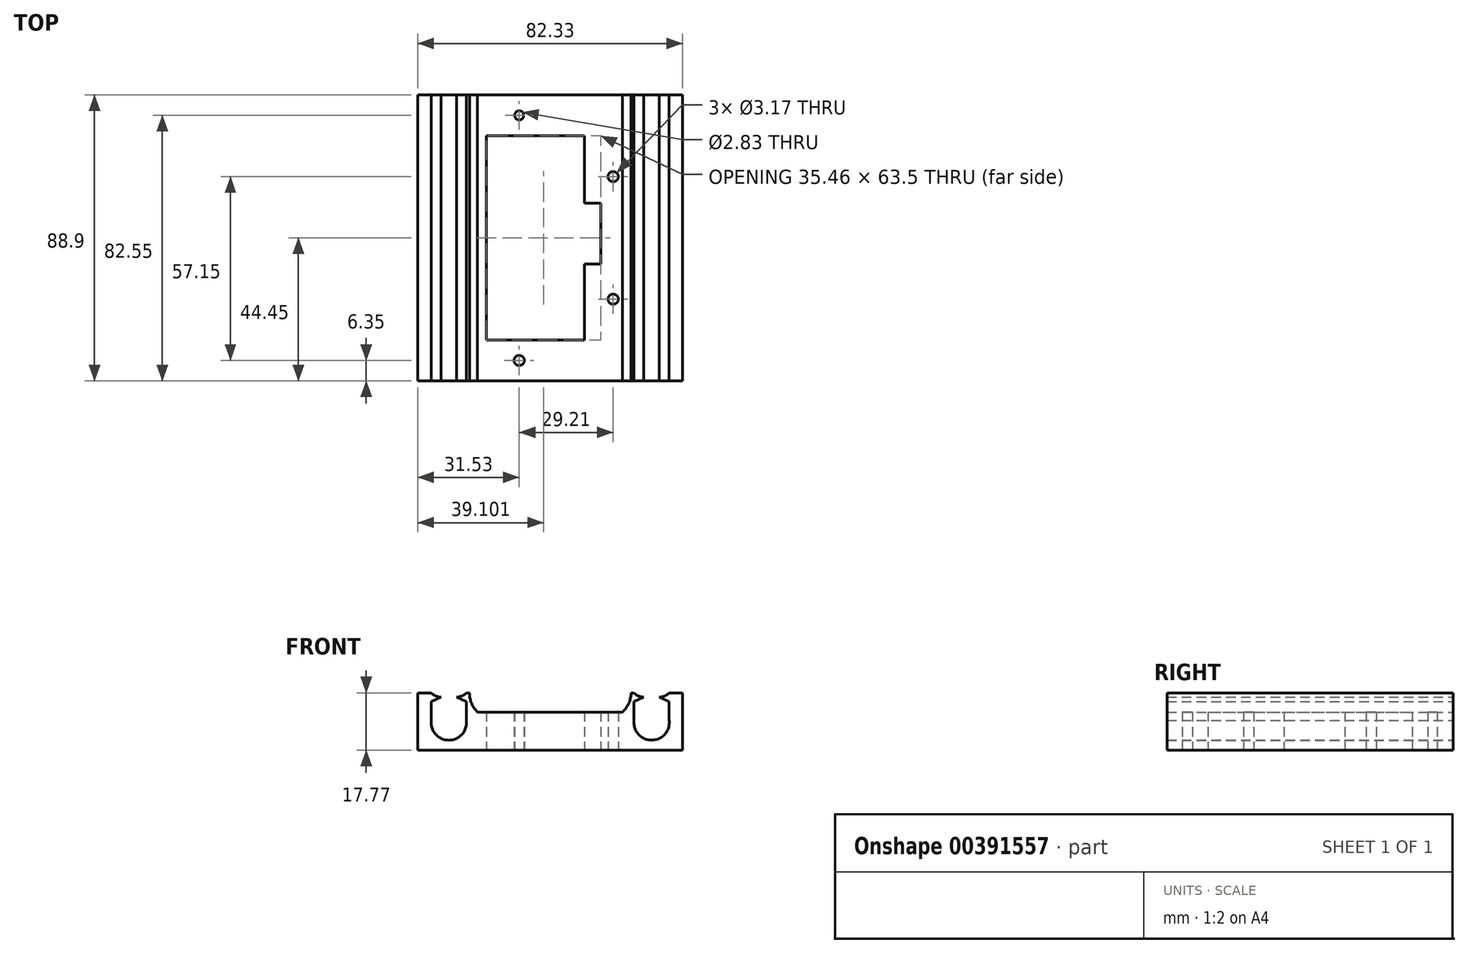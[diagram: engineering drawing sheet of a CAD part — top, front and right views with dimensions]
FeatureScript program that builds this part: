
annotation { "Feature Type Name" : "Feature", "Feature Type Description" : "" }
export const myFeature = defineFeature(function(context is Context, id is Id, definition is map)
    precondition{}
    {
        {
            var Q0;
            Q0=qCreatedBy(makeId("Front.planeOp"),FACE);
            var sketch = newSketch(context, id + "F0", { "sketchPlane" : qUnion([Q0])});
            skLineSegment(sketch, "E0.left", {"start": v(0, 0) * mm, "end": v(0, 17.77) * mm});
            skLineSegment(sketch, "E1", {"start": v(0, 0) * mm, "end": v(-22.84, 0) * mm});
            skLineSegment(sketch, "E2", {"start": v(-78.15, 17.77) * mm, "end": v(-78.15, 9.24) * mm});
            skLineSegment(sketch, "E3", {"start": v(-67.22, 17.77) * mm, "end": v(-67.22, 9.24) * mm});
            skArc(sketch, "E4", {"start": v(-78.15, 9.24) * mm, "mid": v(-72.68, 3.06) * mm, "end": v(-67.22, 9.24) * mm});
            skLineSegment(sketch, "E5", {"start": v(-66.27, 17.77) * mm, "end": v(-66.27, 11.8) * mm});
            skLineSegment(sketch, "E6", {"start": v(-66.27, 11.8) * mm, "end": v(-16.06, 11.8) * mm});
            skLineSegment(sketch, "E7", {"start": v(-16.06, 11.8) * mm, "end": v(-16.06, 17.77) * mm});
            skLineSegment(sketch, "E8", {"start": v(-67.22, 17.77) * mm, "end": v(-66.27, 17.77) * mm});
            skLineSegment(sketch, "E9", {"start": v(-16.06, 17.77) * mm, "end": v(-15.12, 17.77) * mm});
            skLineSegment(sketch, "E10", {"start": v(-15.12, 17.77) * mm, "end": v(-15.12, 9.28) * mm});
            skLineSegment(sketch, "E11", {"start": v(-4.2, 17.77) * mm, "end": v(-4.2, 9.3) * mm});
            skArc(sketch, "E12", {"start": v(-15.12, 9.28) * mm, "mid": v(-9.65, 3.1) * mm, "end": v(-4.2, 9.3) * mm});
            skLineSegment(sketch, "E13", {"start": v(-4.2, 17.77) * mm, "end": v(0, 17.77) * mm});
            skLineSegment(sketch, "E14", {"start": v(0, 17.77) * mm, "end": v(-4.2, 17.77) * mm});
            skLineSegment(sketch, "E15", {"start": v(-78.15, 17.77) * mm, "end": v(-82.33, 17.77) * mm});
            skLineSegment(sketch, "E16", {"start": v(-82.33, 17.77) * mm, "end": v(-82.33, 0) * mm});
            skLineSegment(sketch, "E17", {"start": v(-82.33, 0) * mm, "end": v(0, 0) * mm});
            skArc(sketch, "E18", {"start": v(-18.78, 11.8) * mm, "mid": v(-16.77, 14.5) * mm, "end": v(-16.06, 17.77) * mm});
            skArc(sketch, "E19", {"start": v(-66.27, 17.77) * mm, "mid": v(-65.62, 14.53) * mm, "end": v(-63.76, 11.8) * mm});
            skLineSegment(sketch, "E20", {"start": v(-78.15, 16.48) * mm, "end": v(-75.1, 16.48) * mm});
            skLineSegment(sketch, "E21", {"start": v(-67.22, 16.48) * mm, "end": v(-70.27, 16.48) * mm});
            skLineSegment(sketch, "E22", {"start": v(-75.1, 16.48) * mm, "end": v(-78.15, 15.04) * mm});
            skLineSegment(sketch, "E23", {"start": v(-70.27, 16.48) * mm, "end": v(-67.22, 15.04) * mm});
            skArc(sketch, "E24", {"start": v(-70.27, 16.48) * mm, "mid": v(-68.61, 16.81) * mm, "end": v(-67.22, 17.77) * mm});
            skArc(sketch, "E25", {"start": v(-78.15, 17.77) * mm, "mid": v(-76.76, 16.81) * mm, "end": v(-75.1, 16.48) * mm});
            skLineSegment(sketch, "E26", {"start": v(-4.2, 16.48) * mm, "end": v(-7.25, 16.48) * mm});
            skLineSegment(sketch, "E27", {"start": v(-7.25, 16.48) * mm, "end": v(-4.2, 15.04) * mm});
            skLineSegment(sketch, "E28", {"start": v(-15.12, 16.48) * mm, "end": v(-12.07, 16.48) * mm});
            skLineSegment(sketch, "E29", {"start": v(-12.07, 16.48) * mm, "end": v(-15.12, 15.04) * mm});
            skArc(sketch, "E30", {"start": v(-7.25, 16.48) * mm, "mid": v(-5.6, 16.81) * mm, "end": v(-4.2, 17.77) * mm});
            skArc(sketch, "E31", {"start": v(-15.12, 17.77) * mm, "mid": v(-13.73, 16.81) * mm, "end": v(-12.07, 16.48) * mm});
            skSolve(sketch);
        }
        {
            var Q0;
            Q0 = qSketchRegion(id + "F0", true);
            extrude(context, id + "F1", {"entities" : qUnion([Q0]), "depth" : 88.9 * mm});
        }
        {
            var Q0;
            Q0=qCreatedBy(makeId("Top.planeOp"),FACE);
            var sketch = newSketch(context, id + "F2", { "sketchPlane" : qUnion([Q0])});
            skLineSegment(sketch, "E32", {"start": v(-60.96, -12.7) * mm, "end": v(-60.96, -76.2) * mm});
            skLineSegment(sketch, "E33", {"start": v(-60.96, -76.2) * mm, "end": v(-30.48, -76.2) * mm});
            skLineSegment(sketch, "E34", {"start": v(-30.48, -12.7) * mm, "end": v(-30.48, -76.2) * mm});
            skLineSegment(sketch, "E35", {"start": v(-60.96, -12.7) * mm, "end": v(-30.48, -12.7) * mm});
            skLineSegment(sketch, "E36", {"start": v(-30.48, -12.7) * mm, "end": v(0, -12.7) * mm});
            skLineSegment(sketch, "E37", {"start": v(-30.48, -12.7) * mm, "end": v(-30.48, 0) * mm});
            skLineSegment(sketch, "E38.bottom", {"start": v(-30.48, -33.6) * mm, "end": v(-25.5, -33.6) * mm});
            skLineSegment(sketch, "E38.top", {"start": v(-30.48, -52.58) * mm, "end": v(-25.5, -52.58) * mm});
            skLineSegment(sketch, "E38.left", {"start": v(-30.48, -33.6) * mm, "end": v(-30.48, -52.58) * mm});
            skLineSegment(sketch, "E38.right", {"start": v(-25.5, -33.6) * mm, "end": v(-25.5, -52.58) * mm});
            skSolve(sketch);
        }
        {
            var Q0;
            Q0 = qSketchRegion(id + "F2", true);
            extrude(context, id + "F3", {"entities" : qUnion([Q0]), "operationType" : NewBodyOperationType.REMOVE, "oppositeDirection" : true, "depth" : -127 * mm});
        }
        {
            var Q0;
            Q0=qCreatedBy(makeId("Top.planeOp"),FACE);
            var sketch = newSketch(context, id + "F4", { "sketchPlane" : qUnion([Q0])});
            skCircle(sketch, "E39", {"center": v(-21.59, -25.4) * mm, "radius": 1.59 * mm});
            skCircle(sketch, "E40", {"center": v(-21.59, -63.5) * mm, "radius": 1.59 * mm});
            skSolve(sketch);
        }
        {
            var Q0;
            Q0 = qSketchRegion(id + "F4", true);
            extrude(context, id + "F5", {"entities" : qUnion([Q0]), "operationType" : NewBodyOperationType.REMOVE, "oppositeDirection" : true, "depth" : -127 * mm});
        }
        {
            var Q0;
            Q0=qCreatedBy(makeId("Top.planeOp"),FACE);
            var sketch = newSketch(context, id + "F6", { "sketchPlane" : qUnion([Q0])});
            skCircle(sketch, "E41", {"center": v(-50.8, -6.35) * mm, "radius": 1.42 * mm});
            skCircle(sketch, "E42", {"center": v(-50.8, -82.55) * mm, "radius": 1.59 * mm});
            skSolve(sketch);
        }
        {
            var Q0;
            Q0 = qSketchRegion(id + "F6", true);
            extrude(context, id + "F7", {"entities" : qUnion([Q0]), "operationType" : NewBodyOperationType.REMOVE, "oppositeDirection" : true, "depth" : -76.2 * mm});
        }
    });
